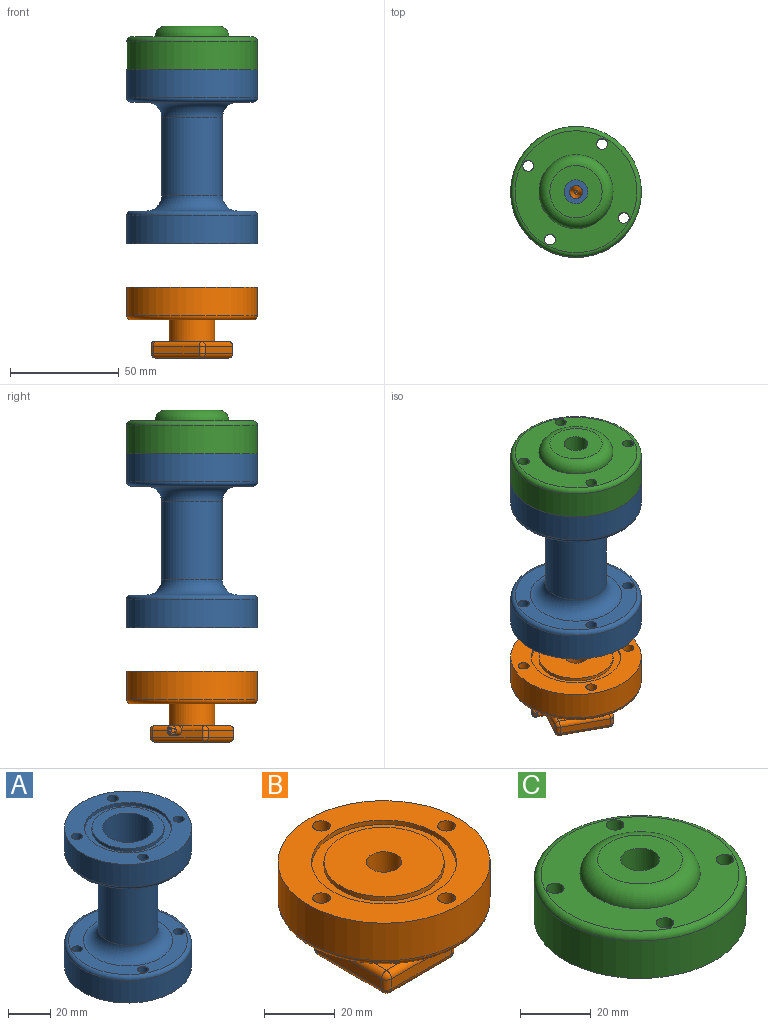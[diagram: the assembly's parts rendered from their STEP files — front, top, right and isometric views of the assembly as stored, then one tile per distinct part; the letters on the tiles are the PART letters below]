
ASSEMBLY  parts=3 mates=5
PART A: 32 faces, bbox 64.9x64.9x80 mm
  f0: plane 34x34mm, normal (0,0,1), area 455.5mm2, adj f10,f29
  f1: cylinder r=2.5mm len=15mm, axis (0,0,-1), area 235.6mm2, adj f9,f23
  f2: cylinder r=2.5mm len=15mm, axis (0,0,-1), area 235.6mm2, adj f9,f23
  f3: cylinder r=2.5mm len=15mm, axis (0,0,-1), area 235.6mm2, adj f9,f23
  f4: cylinder r=2.5mm len=15mm, axis (0,0,-1), area 235.6mm2, adj f9,f23
  f5: cylinder r=30mm len=60mm, axis (0,0,-1), area 2450.4mm2, adj f9,f28
  f6: plane 34x34mm, normal (0,0,-1), area 879.6mm2, adj f17,f21
  f7: cylinder r=11mm len=35mm, axis (0,0,-1), area 2419mm2, adj f8,f20
  f8: plane 24x24mm, normal (0,0,1), area 72.3mm2, adj f7,f10
  f9: plane 60x60mm, normal (0,0,-1), area 1428.6mm2, adj f1,f2,f3,f4,f5,f18
  f10: cylinder r=12mm len=40mm, axis (0,0,-1), area 3015.9mm2, adj f0,f8
  f11: plane 60x60mm, normal (0,0,1), area 1428.6mm2, adj f12,f13,f14,f15,f16,f30
  f12: cylinder r=2.5mm len=15mm, axis (0,0,-1), area 235.6mm2, adj f11,f24
  f13: cylinder r=2.5mm len=15mm, axis (0,0,-1), area 235.6mm2, adj f11,f24
  f14: cylinder r=2.5mm len=15mm, axis (0,0,-1), area 235.6mm2, adj f11,f24
  f15: cylinder r=2.5mm len=15mm, axis (0,0,-1), area 235.6mm2, adj f11,f24
  f16: cylinder r=30mm len=60mm, axis (0,0,-1), area 2450.4mm2, adj f11,f27
  f17: cylinder r=17mm len=34mm, axis (0,0,-1), area 186.9mm2, adj f6,f19
  f18: cylinder r=20.5mm len=41mm, axis (0,0,-1), area 225.4mm2, adj f9,f19
  f19: plane 41x41mm, normal (0,0,-1), area 412.3mm2, adj f17,f18
  f20: plane 22x22mm, normal (0,0,1), area 351.9mm2, adj f7,f21
  f21: cylinder r=3mm len=6mm, axis (0,0,-1), area 94.2mm2, adj f6,f20
  f22: cylinder r=14mm len=36mm, axis (0,0,1), area 3166.7mm2, adj f25,f26
  f23: plane 56x56mm, normal (0,0,1), area 999mm2, adj f1,f2,f3,f4,f26,f28
  f24: plane 56x56mm, normal (0,0,-1), area 999mm2, adj f12,f13,f14,f15,f25,f27
  f25: torus R=21mm, axis (0,0,1), area 1143mm2, adj f22,f24
  f26: torus R=21mm, axis (0,0,1), area 1143mm2, adj f22,f23
  f27: torus R=28mm, axis (0,0,1), area 577.8mm2, adj f16,f24
  f28: torus R=28mm, axis (0,0,1), area 577.8mm2, adj f5,f23
  f29: cylinder r=17mm len=34mm, axis (0,0,1), area 186.9mm2, adj f0,f31
  f30: cylinder r=20.5mm len=41mm, axis (0,0,1), area 225.4mm2, adj f11,f31
  f31: plane 41x41mm, normal (0,0,1), area 412.3mm2, adj f29,f30
PART B: 68 faces, bbox 64.9x64.9x32.5 mm
  f0: plane 0.64x0.05mm, normal (0,0,1), area 0mm2, adj f4,f31,f32,f33
  f1: plane 34x34mm, normal (0,0,1), area 829.4mm2, adj f2,f11
  f2: cylinder r=5mm len=10mm, axis (0,0,1), area 251.3mm2, adj f1,f3
  f3: plane 10x10mm, normal (0,0,1), area 40.1mm2, adj f2,f4
  f4: cone r=3.5mm half-angle=8.4deg, axis (0,0,1), area 242.9mm2, adj f0,f3,f12,f30,f34,f35,f38
  f5: cylinder r=10.5mm len=21mm, axis (0,0,1), area 659.7mm2, adj f6,f13
  f6: plane 56x56mm, normal (0,0,-1), area 2038.1mm2, adj f5,f63,f64,f65,f66,f67
  f7: cylinder r=30mm len=60mm, axis (0,0,1), area 2450.4mm2, adj f8,f63
  f8: plane 60x60mm, normal (0,0,1), area 1428.6mm2, adj f7,f9,f64,f65,f66,f67
  f9: cylinder r=20.5mm len=41mm, axis (0,0,1), area 193.2mm2, adj f8,f10
  f10: plane 41x41mm, normal (0,0,1), area 412.3mm2, adj f9,f11
  f11: cylinder r=17mm len=34mm, axis (0,0,1), area 160.2mm2, adj f1,f10
  f12: plane 0.64x0.05mm, normal (0,0,1), area 0mm2, adj f4,f36,f37,f39
  f13: plane 26x26mm, normal (0,0,1), area 280mm2, adj f5,f41,f43,f44,f45,f46,f47,f59
  f14: plane 26x3.5mm, normal (-1,0,0), area 91mm2, adj f55,f58,f59,f62
  f15: plane 26x24mm, normal (0,0,-1), area 624mm2, adj f40,f42,f54,f58
  f16: plane 26x3.5mm, normal (1,0,0), area 81.9mm2, adj f21,f46,f47,f50,f51,f54
  f17: plane 24x3.5mm, normal (0,-1,0), area 84mm2, adj f42,f43,f50,f62
  f18: plane 24x3.5mm, normal (0,1,0), area 84mm2, adj f40,f41,f51,f55
  f19: plane 2.25x2.05mm, normal (0,-1,0), area 1.7mm2, adj f25,f26,f27,f28,f29,f32
  f20: plane 2.25x2.05mm, normal (0,1,0), area 1.7mm2, adj f25,f26,f27,f28,f29,f37
  f21: cylinder r=2.25mm len=6mm, axis (1,0,0), area 78.4mm2, adj f16,f22,f23,f44,f45
  f22: bspline ~4.5x2.25mm, area 7.5mm2, adj f21,f24
  f23: bspline ~4.5x2.25mm, area 7.5mm2, adj f21,f24
  f24: cylinder r=2.25mm len=4.5mm, axis (0,0,-1), area 9.5mm2, adj f22,f23,f27
  f25: cylinder r=0.75mm len=2mm, axis (0,0,-1), area 4.4mm2, adj f19,f20,f26,f33,f34,f38,f39
  f26: torus R=0.25mm, axis (0,-1,0), area 2.7mm2, adj f19,f20,f25,f27
  f27: cylinder r=0.75mm len=21mm, axis (1,0,0), area 93.9mm2, adj f19,f20,f24,f26,f28
  f28: torus R=1.75mm, axis (0,-1,0), area 4.7mm2, adj f19,f20,f27,f29
  f29: cylinder r=0.75mm len=1.5mm, axis (0,0,1), area 0.9mm2, adj f19,f20,f28,f30,f31,f35,f36
  f30: bspline ~0.96x0.72mm, area 0.2mm2, adj f4,f29,f31
  f31: torus R=0.95mm, axis (0,0,1), area 0mm2, adj f0,f29,f30,f32
  f32: cylinder r=0.2mm len=0.5mm, axis (1,0,0), area 0.2mm2, adj f0,f19,f31,f33
  f33: torus R=0.95mm, axis (0,0,1), area 0mm2, adj f0,f25,f32,f34
  f34: bspline ~0.95x0.69mm, area 0.2mm2, adj f4,f25,f33
  f35: bspline ~0.96x0.72mm, area 0.2mm2, adj f4,f29,f36
  f36: torus R=0.95mm, axis (0,0,1), area 0mm2, adj f12,f29,f35,f37
  f37: cylinder r=0.2mm len=0.5mm, axis (-1,0,0), area 0.2mm2, adj f12,f20,f36,f39
  f38: bspline ~0.96x0.72mm, area 0.2mm2, adj f4,f25,f39
  f39: torus R=0.95mm, axis (0,0,1), area 0mm2, adj f12,f25,f37,f38
  f40: cylinder r=2mm len=24mm, axis (1,0,0), area 75.4mm2, adj f15,f18,f53,f56
  f41: cylinder r=2mm len=24mm, axis (-1,0,0), area 75.4mm2, adj f13,f18,f49,f57
  f42: cylinder r=2mm len=24mm, axis (-1,0,0), area 75.4mm2, adj f15,f17,f52,f60
  f43: cylinder r=2mm len=24mm, axis (1,0,0), area 75.4mm2, adj f13,f17,f48,f61
  f44: bspline ~2.46x2.03mm, area 3.8mm2, adj f13,f21,f46
  f45: bspline ~2.46x2.03mm, area 3.8mm2, adj f13,f21,f47
  f46: cylinder r=2mm len=10.76mm, axis (0,1,0), area 33.8mm2, adj f13,f16,f44,f48
  f47: cylinder r=2mm len=10.76mm, axis (0,1,0), area 33.8mm2, adj f13,f16,f45,f49
  f48: sphere r=2mm, area 6.3mm2, adj f43,f46,f50
  f49: sphere r=2mm, area 6.3mm2, adj f41,f47,f51
  f50: cylinder r=2mm len=3.5mm, axis (0,0,-1), area 11mm2, adj f16,f17,f48,f52
  f51: cylinder r=2mm len=3.5mm, axis (0,0,1), area 11mm2, adj f16,f18,f49,f53
  f52: sphere r=2mm, area 6.3mm2, adj f42,f50,f54
  f53: sphere r=2mm, area 6.3mm2, adj f40,f51,f54
  f54: cylinder r=2mm len=26mm, axis (0,1,0), area 81.7mm2, adj f15,f16,f52,f53
  f55: cylinder r=2mm len=3.5mm, axis (0,0,-1), area 11mm2, adj f14,f18,f56,f57
  f56: sphere r=2mm, area 6.3mm2, adj f40,f55,f58
  f57: sphere r=2mm, area 6.3mm2, adj f41,f55,f59
  f58: cylinder r=2mm len=26mm, axis (0,1,0), area 81.7mm2, adj f14,f15,f56,f60
  f59: cylinder r=2mm len=26mm, axis (0,1,0), area 81.7mm2, adj f13,f14,f57,f61
  f60: sphere r=2mm, area 6.3mm2, adj f42,f58,f62
  f61: sphere r=2mm, area 6.3mm2, adj f43,f59,f62
  f62: cylinder r=2mm len=3.5mm, axis (0,0,1), area 11mm2, adj f14,f17,f60,f61
  f63: torus R=28mm, axis (0,0,1), area 577.8mm2, adj f6,f7
  f64: cylinder r=2.5mm len=15mm, axis (0,0,1), area 235.6mm2, adj f6,f8
  f65: cylinder r=2.5mm len=15mm, axis (0,0,1), area 235.6mm2, adj f6,f8
  f66: cylinder r=2.5mm len=15mm, axis (0,0,1), area 235.6mm2, adj f6,f8
  f67: cylinder r=2.5mm len=15mm, axis (0,0,1), area 235.6mm2, adj f6,f8
PART C: 15 faces, bbox 64.9x64.9x20 mm
  f0: plane 34x34mm, normal (0,0,-1), area 812.9mm2, adj f8,f11
  f1: plane 56x56mm, normal (0,0,1), area 1476.5mm2, adj f3,f4,f5,f6,f13,f14
  f2: plane 60x60mm, normal (0,0,-1), area 1428.6mm2, adj f3,f4,f5,f6,f7,f9
  f3: cylinder r=2.5mm len=15mm, axis (0,0,-1), area 235.6mm2, adj f1,f2
  f4: cylinder r=2.5mm len=15mm, axis (0,0,-1), area 235.6mm2, adj f1,f2
  f5: cylinder r=2.5mm len=15mm, axis (0,0,-1), area 235.6mm2, adj f1,f2
  f6: cylinder r=2.5mm len=15mm, axis (0,0,-1), area 235.6mm2, adj f1,f2
  f7: cylinder r=30mm len=60mm, axis (0,0,-1), area 2450.4mm2, adj f2,f13
  f8: cylinder r=17mm len=34mm, axis (0,0,-1), area 186.9mm2, adj f0,f10
  f9: cylinder r=20.5mm len=41mm, axis (0,0,-1), area 225.4mm2, adj f2,f10
  f10: plane 41x41mm, normal (0,0,-1), area 412.3mm2, adj f8,f9
  f11: cylinder r=5.5mm len=20mm, axis (0,0,-1), area 691.2mm2, adj f0,f12
  f12: plane 24x24mm, normal (0,0,1), area 357.4mm2, adj f11,f14
  f13: torus R=28mm, axis (0,0,1), area 577.8mm2, adj f1,f7
  f14: torus R=12mm, axis (0,0,1), area 749.3mm2, adj f1,f12
PLACE A t=(19.7,-40.65,-126)mm
PLACE B rot(axis=(0,0,1),151.4deg) t=(19.7,-40.65,-146)mm
PLACE C t=(19.7,-40.65,-46)mm
MATE cylindrical C.f3 <-> A.f1  axis (0,0,-1) through (7.73,-62.6,-46)mm
MATE cylindrical B.f67 <-> A.f2  axis (0,0,1) through (41.65,-52.62,-146)mm
MATE planar B.f2 <-> A.f4  axis (0,0,1) through (19.7,-40.65,-146)mm
MATE planar C.f5 <-> A.f3  axis (0,0,-1) through (31.67,-18.71,-46)mm
MATE cylindrical B.f65 <-> A.f4  axis (0,0,1) through (-2.25,-28.69,-146)mm
